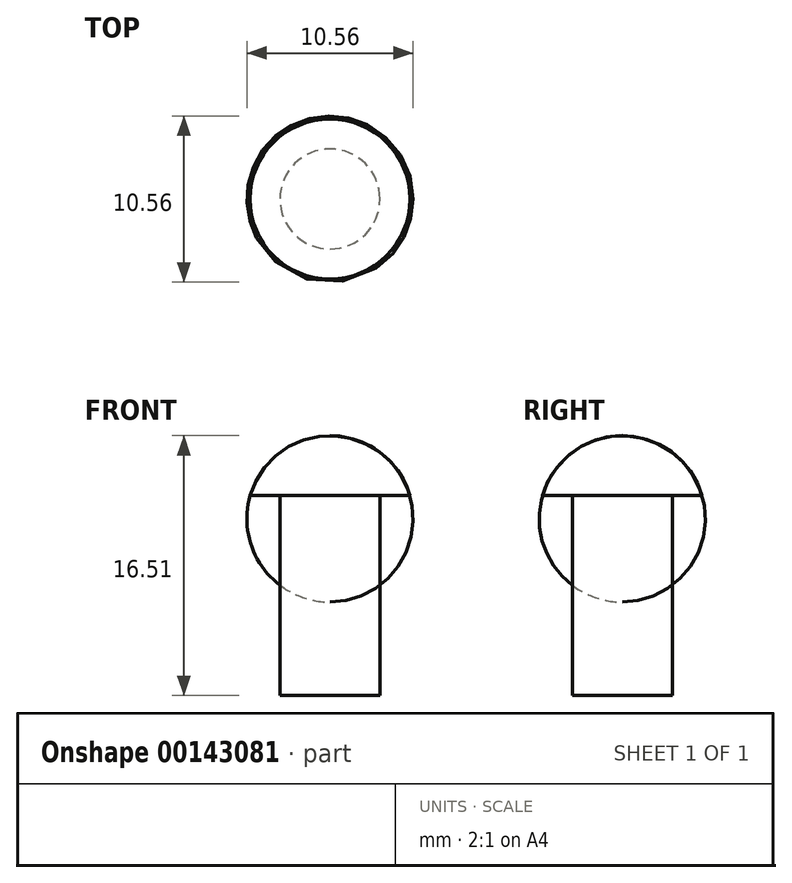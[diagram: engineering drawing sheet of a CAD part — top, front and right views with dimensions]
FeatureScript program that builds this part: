
annotation { "Feature Type Name" : "Feature", "Feature Type Description" : "" }
export const myFeature = defineFeature(function(context is Context, id is Id, definition is map)
    precondition{}
    {
        {
            var Q0;
            Q0=qCreatedBy(makeId("Front.planeOp"),FACE);
            var sketch = newSketch(context, id + "F0", { "sketchPlane" : qUnion([Q0])});
            skLineSegment(sketch, "E0", {"start": v(0, 0) * mm, "end": v(0, 16.51) * mm});
            skLineSegment(sketch, "E1", {"start": v(0, 0) * mm, "end": v(3.18, 0) * mm});
            skLineSegment(sketch, "E2", {"start": v(3.18, 0) * mm, "end": v(3.18, 12.7) * mm});
            skLineSegment(sketch, "E3", {"start": v(3.18, 12.7) * mm, "end": v(5.08, 12.7) * mm});
            skArc(sketch, "E4", {"start": v(5.08, 12.7) * mm, "mid": v(3.18, 15.45) * mm, "end": v(0, 16.51) * mm});
            skSolve(sketch);
        }
        {
            var Q0;
            Q0=makeQuery(id+"F0.imprint","IMPRINT",FACE,{"disambiguationData":[TD([[makeQuery(id+"F0.imprint","IMPRINT",EDGE,{"derivedFrom":sQuery(id+"F0.wireOp",EDGE,"E0")}),-1.0]])]});
            var Q1;
            Q1=sQuery(id+"F0.wireOp",EDGE,"E0");
            revolve(context, id + "F1", {"entities" : qUnion([Q0]), "axis" : qUnion([Q1]), "revolveType" : RevolveType.FULL});
        }
    });
